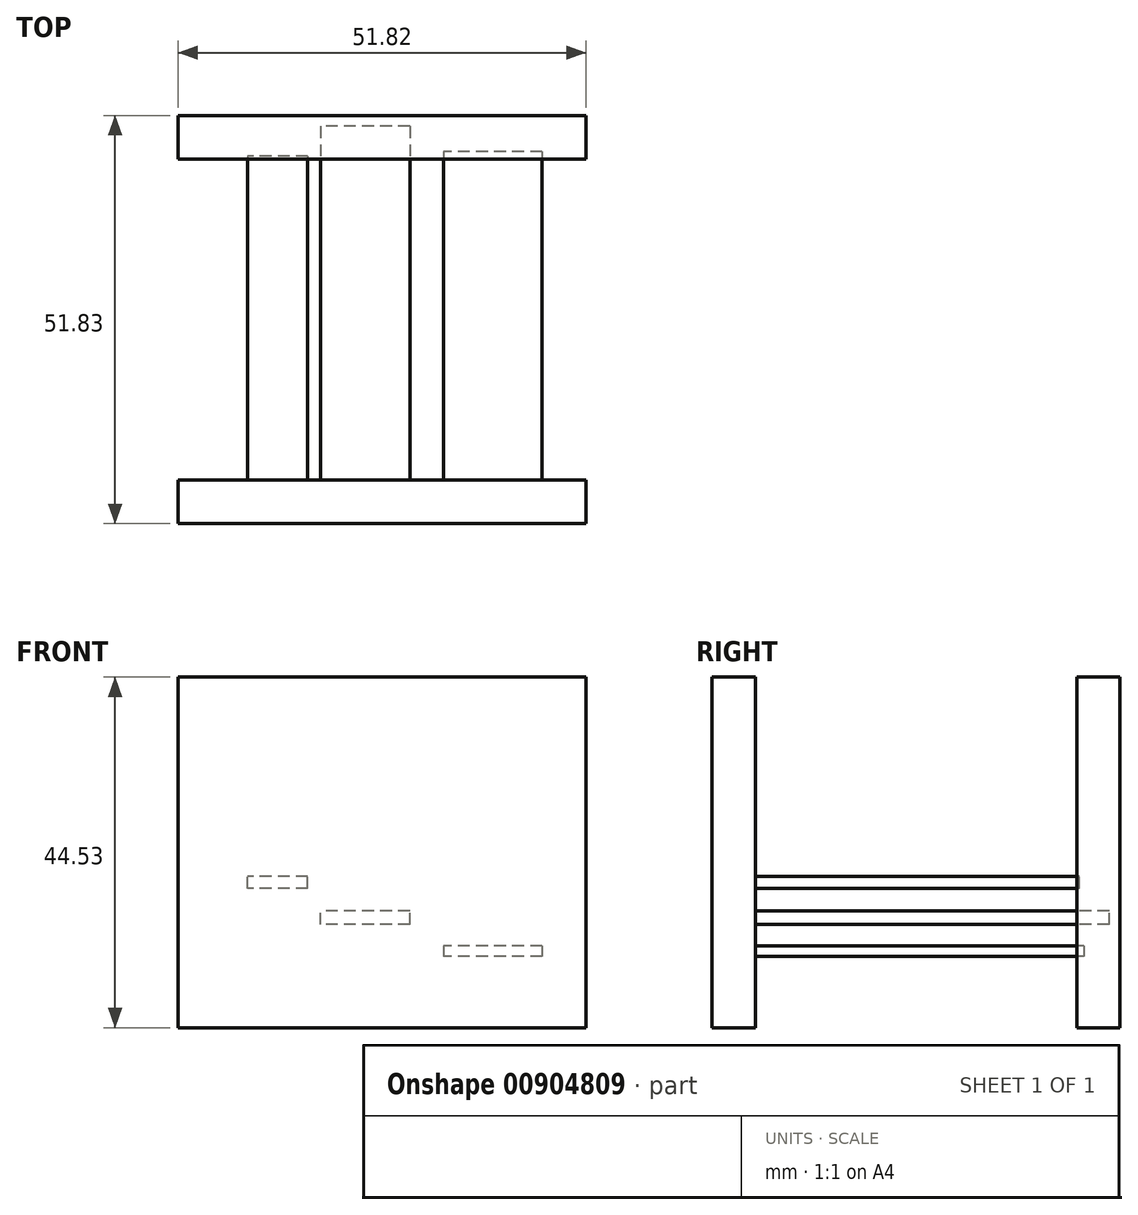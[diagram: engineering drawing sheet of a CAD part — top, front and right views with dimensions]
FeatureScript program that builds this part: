
annotation { "Feature Type Name" : "Feature", "Feature Type Description" : "" }
export const myFeature = defineFeature(function(context is Context, id is Id, definition is map)
    precondition{}
    {
        {
            var Q0;
            Q0=qCreatedBy(makeId("Right.planeOp"),FACE);
            var sketch = newSketch(context, id + "F0", { "sketchPlane" : qUnion([Q0])});
            skLineSegment(sketch, "E0", {"start": v(-20.2, 20.6) * mm, "end": v(-20.2, -23.94) * mm});
            skLineSegment(sketch, "E1", {"start": v(-20.2, -23.94) * mm, "end": v(-25.72, -23.94) * mm});
            skLineSegment(sketch, "E2", {"start": v(-25.72, -23.94) * mm, "end": v(-25.72, 20.6) * mm});
            skLineSegment(sketch, "E3", {"start": v(-25.72, 20.6) * mm, "end": v(-20.2, 20.6) * mm});
            skLineSegment(sketch, "E4", {"start": v(26.11, 20.6) * mm, "end": v(26.11, -23.94) * mm});
            skLineSegment(sketch, "E5", {"start": v(26.11, -23.94) * mm, "end": v(20.6, -23.94) * mm});
            skLineSegment(sketch, "E6", {"start": v(20.6, -23.94) * mm, "end": v(20.6, 20.6) * mm});
            skLineSegment(sketch, "E7", {"start": v(20.6, 20.6) * mm, "end": v(26.11, 20.6) * mm});
            skSolve(sketch);
        }
        {
            var Q0;
            Q0=makeQuery(id+"F0.imprint","IMPRINT",FACE,{"disambiguationData":[TD([[makeQuery(id+"F0.imprint","IMPRINT",EDGE,{"derivedFrom":sQuery(id+"F0.wireOp",EDGE,"E4")}),-1.0]])]});
            var Q1;
            Q1=makeQuery(id+"F0.imprint","IMPRINT",FACE,{"disambiguationData":[TD([[makeQuery(id+"F0.imprint","IMPRINT",EDGE,{"derivedFrom":sQuery(id+"F0.wireOp",EDGE,"E0")}),-1.0]])]});
            extrude(context, id + "F1", {"entities" : qUnion([Q0, Q1]), "depth" : 51.82 * mm, "offsetDistance" : 25.4 * mm});
        }
        {
            var Q0;
            Q0=makeQuery(id+"F1.opExtrude","SWEPT_FACE",FACE,{"disambiguationData":[OSD([sQuery(id+"F0.wireOp",EDGE,"E0")])]});
            var sketch = newSketch(context, id + "F2", { "sketchPlane" : qUnion([Q0])});
            skLineSegment(sketch, "E8.bottom", {"start": v(-46.24, -13.57) * mm, "end": v(-33.73, -13.57) * mm});
            skLineSegment(sketch, "E8.top", {"start": v(-46.24, -14.9) * mm, "end": v(-33.73, -14.9) * mm});
            skLineSegment(sketch, "E8.left", {"start": v(-46.24, -13.57) * mm, "end": v(-46.24, -14.9) * mm});
            skLineSegment(sketch, "E8.right", {"start": v(-33.73, -13.57) * mm, "end": v(-33.73, -14.9) * mm});
            skSolve(sketch);
        }
        {
            var Q0;
            Q0 = qSketchRegion(id + "F2", true);
            extrude(context, id + "F3", {"entities" : qUnion([Q0]), "depth" : 41.73 * mm, "offsetDistance" : 25.4 * mm});
        }
        {
            var Q0;
            Q0=makeQuery(id+"F1.opExtrude","SWEPT_FACE",FACE,{"disambiguationData":[OSD([sQuery(id+"F0.wireOp",EDGE,"E0")])]});
            var sketch = newSketch(context, id + "F4", { "sketchPlane" : qUnion([Q0])});
            skLineSegment(sketch, "E9.bottom", {"start": v(-29.46, -10.85) * mm, "end": v(-18.07, -10.85) * mm});
            skLineSegment(sketch, "E9.top", {"start": v(-29.46, -9.09) * mm, "end": v(-18.07, -9.09) * mm});
            skLineSegment(sketch, "E9.left", {"start": v(-29.46, -10.85) * mm, "end": v(-29.46, -9.09) * mm});
            skLineSegment(sketch, "E9.right", {"start": v(-18.07, -10.85) * mm, "end": v(-18.07, -9.09) * mm});
            skSolve(sketch);
        }
        {
            var Q0;
            Q0=makeQuery(id+"F4.imprint","IMPRINT",FACE,{"disambiguationData":[TD([[makeQuery(id+"F4.imprint","IMPRINT",EDGE,{"derivedFrom":sQuery(id+"F4.wireOp",EDGE,"E9.bottom")}),1.0]])]});
            extrude(context, id + "F5", {"entities" : qUnion([Q0]), "depth" : 44.96 * mm, "offsetDistance" : 25.4 * mm});
        }
        {
            var Q0;
            Q0=makeQuery(id+"F1.opExtrude","SWEPT_FACE",FACE,{"disambiguationData":[OSD([sQuery(id+"F0.wireOp",EDGE,"E0")])]});
            var sketch = newSketch(context, id + "F6", { "sketchPlane" : qUnion([Q0])});
            skLineSegment(sketch, "E10.bottom", {"start": v(-16.47, -6.28) * mm, "end": v(-8.85, -6.28) * mm});
            skLineSegment(sketch, "E10.top", {"start": v(-16.47, -4.71) * mm, "end": v(-8.85, -4.71) * mm});
            skLineSegment(sketch, "E10.left", {"start": v(-16.47, -6.28) * mm, "end": v(-16.47, -4.71) * mm});
            skLineSegment(sketch, "E10.right", {"start": v(-8.85, -6.28) * mm, "end": v(-8.85, -4.71) * mm});
            skSolve(sketch);
        }
        {
            var Q0;
            Q0 = qSketchRegion(id + "F6", true);
            extrude(context, id + "F7", {"entities" : qUnion([Q0]), "depth" : 41.17 * mm, "offsetDistance" : 25.4 * mm});
        }
    });
